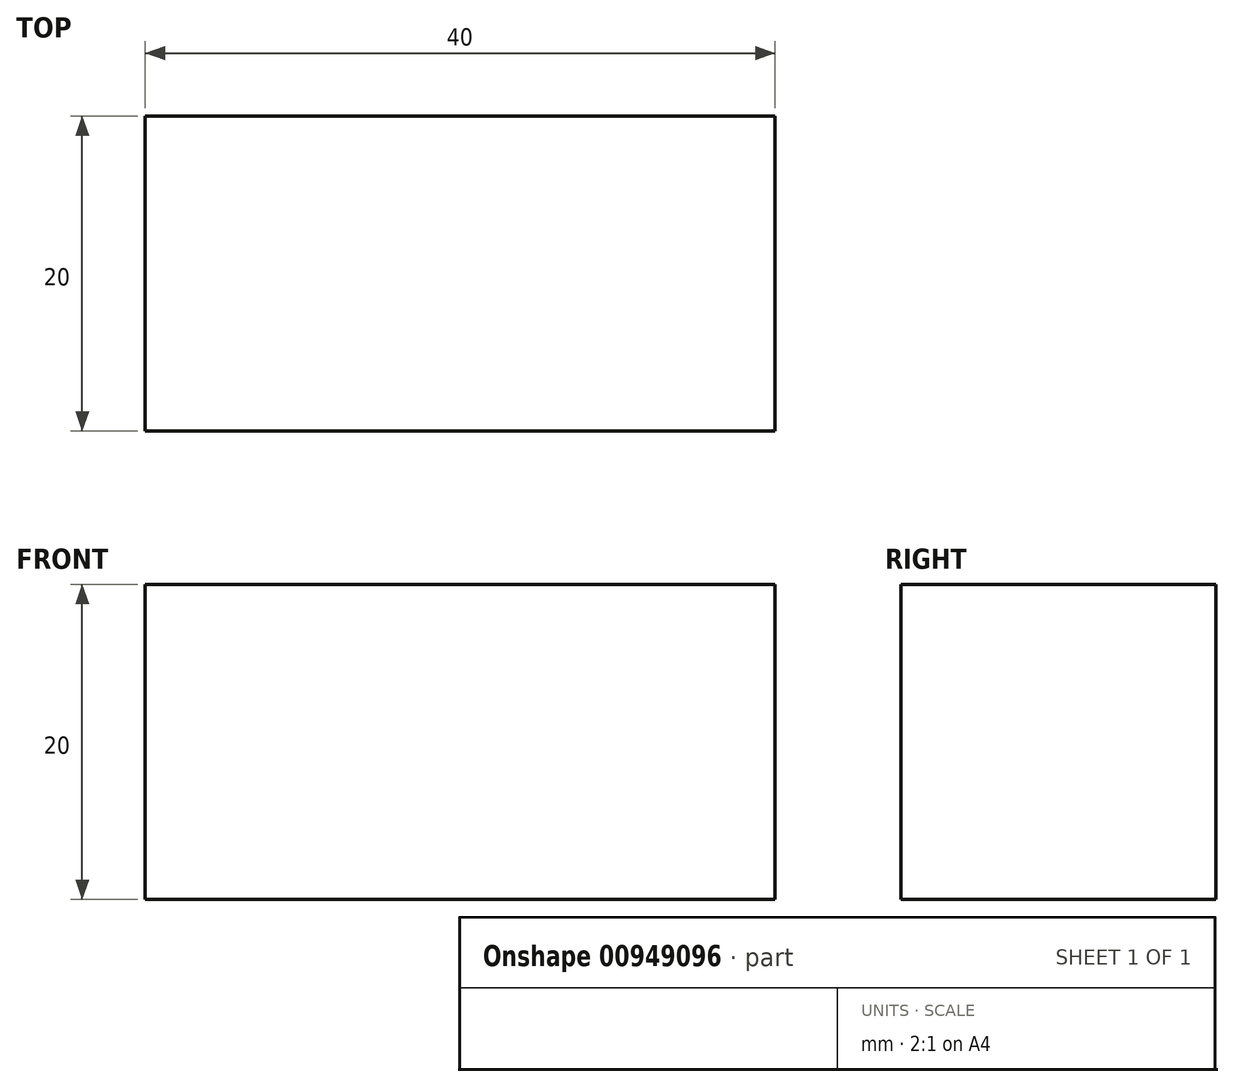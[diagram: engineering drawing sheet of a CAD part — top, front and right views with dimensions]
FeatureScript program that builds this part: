
annotation { "Feature Type Name" : "Feature", "Feature Type Description" : "" }
export const myFeature = defineFeature(function(context is Context, id is Id, definition is map)
    precondition{}
    {
        {
            var Q0;
            Q0=qCreatedBy(makeId("Front.planeOp"),FACE);
            var sketch = newSketch(context, id + "F0", { "sketchPlane" : qUnion([Q0])});
            skLineSegment(sketch, "E0.bottom", {"start": v(0, 0) * mm, "end": v(-40, 0) * mm});
            skLineSegment(sketch, "E0.top", {"start": v(0, 20) * mm, "end": v(-40, 20) * mm});
            skLineSegment(sketch, "E0.left", {"start": v(0, 0) * mm, "end": v(0, 20) * mm});
            skLineSegment(sketch, "E0.right", {"start": v(-40, 0) * mm, "end": v(-40, 20) * mm});
            skSolve(sketch);
        }
        {
            var Q0;
            Q0=makeQuery(id+"F0.imprint","IMPRINT",FACE,{"disambiguationData":[TD([[makeQuery(id+"F0.imprint","IMPRINT",EDGE,{"derivedFrom":sQuery(id+"F0.wireOp",EDGE,"E0.bottom")}),-1.0]])]});
            extrude(context, id + "F1", {"entities" : qUnion([Q0]), "depth" : 20 * mm, "offsetDistance" : 25 * mm});
        }
    });
